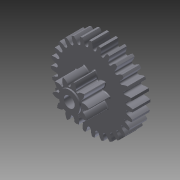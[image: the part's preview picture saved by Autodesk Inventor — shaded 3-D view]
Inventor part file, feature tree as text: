
AUTODESK INVENTOR PART (.ipt)
format: ipt  version: 2013 (Build 170138000, 138)  size: 1,772,032 bytes
history: native  units: in
note: dims shown in document units (in); Inventor stores cm internally (conversion verified against a paired STEP export)
features: sketch x4, extrude x4, fillet x1, hole x1
ambient origin geometry x8: Origin, YZ Plane, XZ Plane, XY Plane, X Axis, Y Axis, Z Axis, Center Point
bodies: Solid1 (feature_tree)
feature tree (10):
  sketch  "Sketch1"  dims[d0=0.118in d1=0.0in d2=0.008in d3=0.0in]
  extrude  "Extrusion1"  Depth=0.008in TaperAngle=0.0deg
  extrude  "Extrusion2"  Depth=0.138in
  extrude  "Extrusion3"  Depth=0.005in
  extrude  "Extrusion4"  [1 undecoded]
  fillet  "Fillet1"  [1 undecoded]
  hole  "Hole1"  [1 undecoded]
  sketch  "Sketch2"  dims[d4=0.098in d5=0.0in d6=0.138in]
  sketch  "Sketch3"  dims[d7=0.008in d8=0.0in d9=0.005in]
  sketch  "Sketch4"  dims[d10=0.061in d11=0.75in d12=0.375in d13=0.25in d14=0.5635in d15=1.0in d16=0.8108in]
note: 3 required parameter values undecoded (feature->parameter linkage not recoverable at this tier; creation-order binding heuristic only, values carry confidence <= 0.55)
